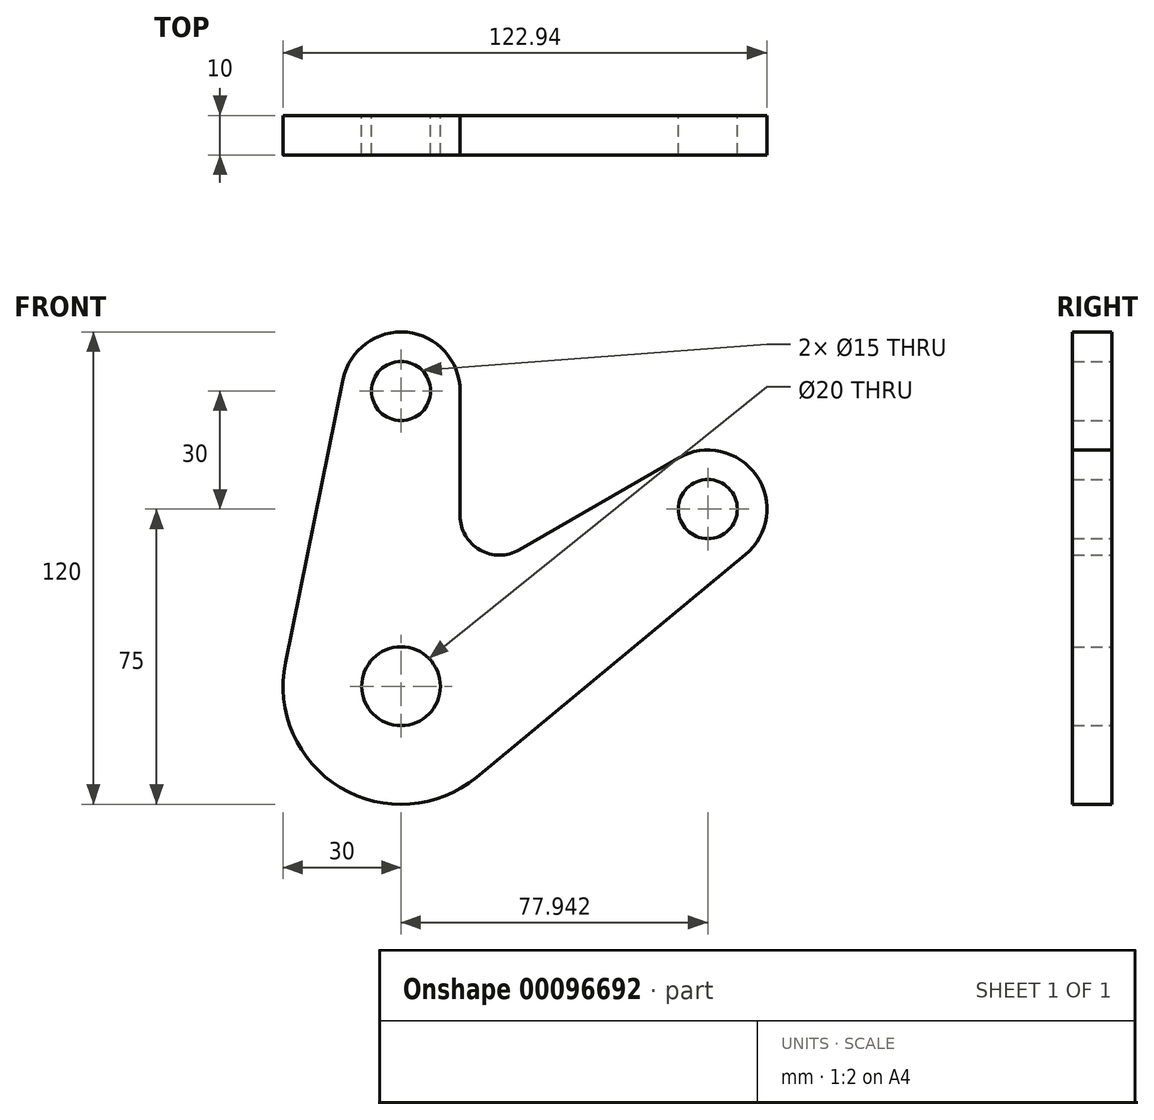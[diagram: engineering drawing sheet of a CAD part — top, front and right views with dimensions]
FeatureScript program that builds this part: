
annotation { "Feature Type Name" : "Feature", "Feature Type Description" : "" }
export const myFeature = defineFeature(function(context is Context, id is Id, definition is map)
    precondition{}
    {
        {
            var Q0;
            Q0=qCreatedBy(makeId("Front.planeOp"),FACE);
            var sketch = newSketch(context, id + "F0", { "sketchPlane" : qUnion([Q0])});
            skCircle(sketch, "E0", {"center": v(0, 0) * mm, "radius": 10 * mm});
            skCircle(sketch, "E1", {"center": v(0, 75) * mm, "radius": 7.5 * mm});
            skCircle(sketch, "E2", {"center": v(77.94, 45) * mm, "radius": 7.5 * mm});
            skLineSegment(sketch, "E3", {"start": v(0, 0) * mm, "end": v(77.94, 45) * mm, "construction": true});
            skLineSegment(sketch, "E4", {"start": v(0, 0) * mm, "end": v(0, 75) * mm, "construction": true});
            skPoint(sketch, "E5", {"position": v(38.97, 22.5) * mm});
            skLineSegment(sketch, "E6", {"start": v(19.12, -23.12) * mm, "end": v(87.5, 33.44) * mm});
            skArc(sketch, "E7", {"start": v(19.12, -23.12) * mm, "mid": v(-15.44, -25.72) * mm, "end": v(-29.4, 6) * mm});
            skLineSegment(sketch, "E8", {"start": v(-29.4, 6) * mm, "end": v(-14.7, 78) * mm});
            skLineSegment(sketch, "E9", {"start": v(30, 34.64) * mm, "end": v(70.44, 58) * mm});
            skLineSegment(sketch, "E10", {"start": v(15, 75) * mm, "end": v(15, 43.3) * mm});
            skArc(sketch, "E11", {"start": v(15, 75) * mm, "mid": v(1.5, 89.92) * mm, "end": v(-14.7, 78) * mm});
            skArc(sketch, "E12", {"start": v(15, 43.3) * mm, "mid": v(20, 34.64) * mm, "end": v(30, 34.64) * mm});
            skArc(sketch, "E13", {"start": v(70.44, 58) * mm, "mid": v(90.26, 53.56) * mm, "end": v(87.5, 33.44) * mm});
            skSolve(sketch);
        }
        {
            var Q0;
            Q0 = qSketchRegion(id + "F0", true);
            extrude(context, id + "F1", {"entities" : qUnion([Q0]), "depth" : 10 * mm});
        }
    });
